SOLIDWORKS PART (.sldprt)
format: sldprt  version: not decoded by parser v0  size: 148,992 bytes
history: native  units: mm
features: sketch x3, extrude x3, pattern_linear x2, fillet x2, material x1 (+11 scaffold rows collapsed)
feature tree (22):
  scaffold x11  (default folders/planes/origin — collapsed)
  material  "Material <not specified>"
  sketch  "Sketch1"
  extrude  "Boss-Extrude1"  [1 undecoded]
  sketch  "Sketch2"  dims[D1=10.0mm]
  extrude  "Boss-Extrude2"  Depth=1mm
  pattern_linear  "LPattern1"  Count1=2 Count2=1 Spacing1=22mm Spacing2=10mm
  pattern_linear  "LPattern2"  Count1=2 Count2=1 Spacing1=10mm Spacing2=10mm
  sketch  "Sketch3"  dims[D1=0.9mm]
  extrude  "Boss-Extrude3"  Depth=1.5mm
  fillet  "Fillet4"  Radius=0.25mm
  fillet  "Fillet5"  Radius=0.25mm
decode coverage: 8 of 10 modeling features carry decoded parameters
note: 1 parameter value undecoded
note: suppression state not decoded; provenance and decode notes live in map.json
